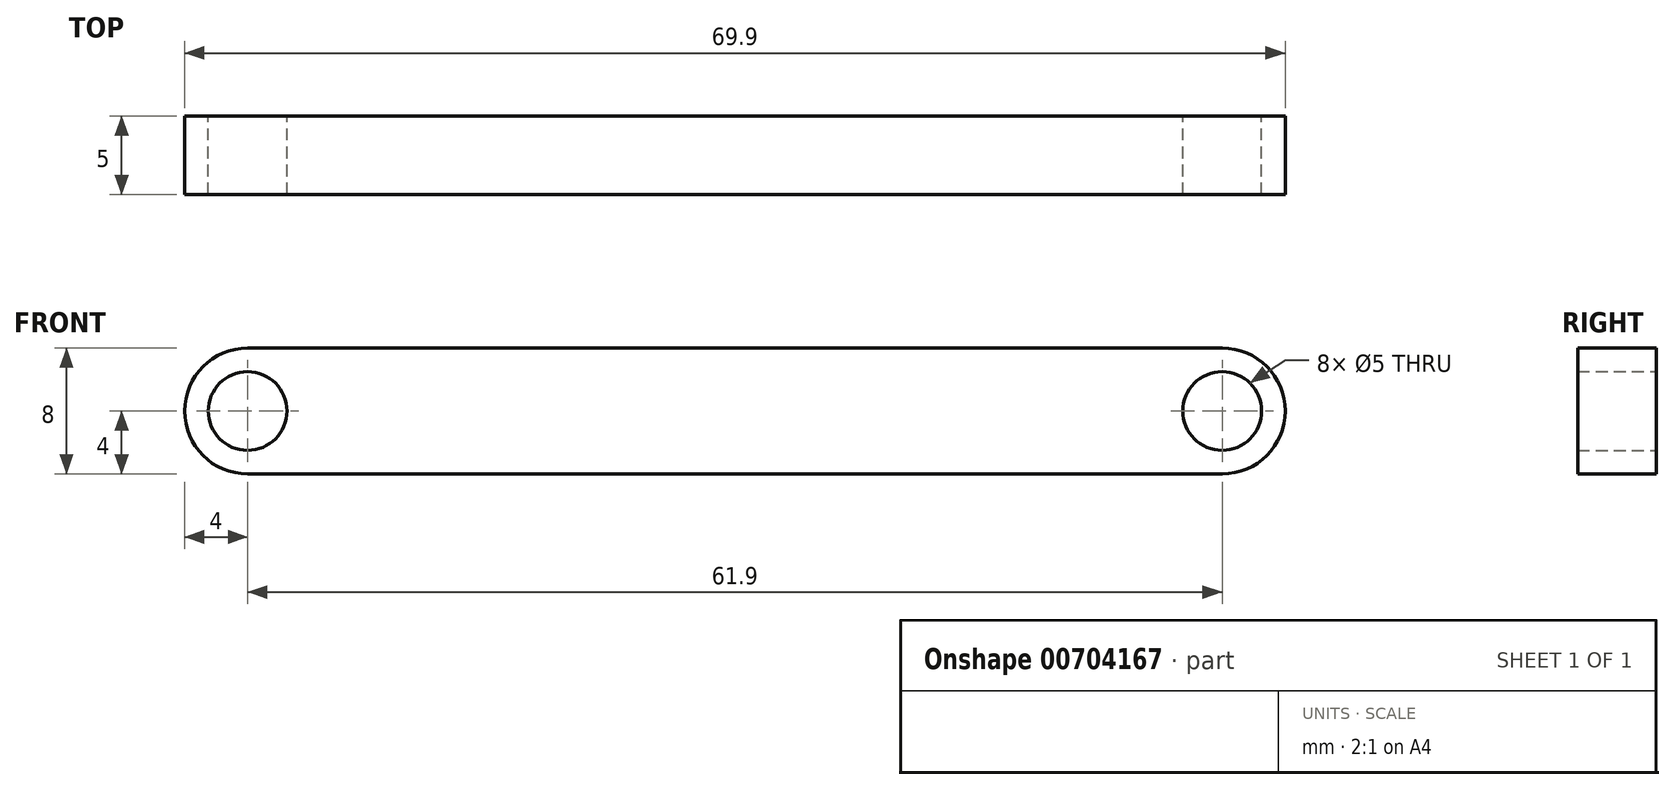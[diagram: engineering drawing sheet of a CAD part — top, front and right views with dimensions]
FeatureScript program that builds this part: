
annotation { "Feature Type Name" : "Feature", "Feature Type Description" : "" }
export const myFeature = defineFeature(function(context is Context, id is Id, definition is map)
    precondition{}
    {
        {
            var Q0;
            Q0=qCreatedBy(makeId("Front.planeOp"),FACE);
            var sketch = newSketch(context, id + "F0", { "sketchPlane" : qUnion([Q0])});
            skLineSegment(sketch, "E0.bottom", {"start": v(-30.95, 4) * mm, "end": v(0, 4) * mm});
            skLineSegment(sketch, "E0.top", {"start": v(-30.95, -4) * mm, "end": v(0, -4) * mm});
            skLineSegment(sketch, "E0.left", {"start": v(-30.95, 4) * mm, "end": v(-30.95, -4) * mm, "construction": true});
            skLineSegment(sketch, "E0.right", {"start": v(0, 4) * mm, "end": v(0, -4) * mm});
            skArc(sketch, "E1", {"start": v(-30.95, -4) * mm, "mid": v(-34.95, 0) * mm, "end": v(-30.95, 4) * mm});
            skCircle(sketch, "E2", {"center": v(-30.95, 0) * mm, "radius": 2.5 * mm});
            skLineSegment(sketch, "E3.MirrorCS", {"start": v(30.95, -4) * mm, "end": v(0, -4) * mm});
            skArc(sketch, "E4.MirrorCS", {"start": v(30.95, -4) * mm, "mid": v(34.95, 0) * mm, "end": v(30.95, 4) * mm});
            skCircle(sketch, "E5.MirrorC", {"center": v(30.95, 0) * mm, "radius": 2.5 * mm});
            skLineSegment(sketch, "E6.MirrorCS", {"start": v(30.95, 4) * mm, "end": v(0, 4) * mm});
            skSolve(sketch);
        }
        {
            var Q0;
            Q0=makeQuery(id+"F0.imprint","IMPRINT",FACE,{"disambiguationData":[TD([[makeQuery(id+"F0.imprint","IMPRINT",EDGE,{"derivedFrom":sQuery(id+"F0.wireOp",EDGE,"E0.bottom")}),-1.0]])]});
            var Q1;
            Q1=makeQuery(id+"F0.imprint","IMPRINT",FACE,{"disambiguationData":[TD([[makeQuery(id+"F0.imprint","IMPRINT",EDGE,{"derivedFrom":sQuery(id+"F0.wireOp",EDGE,"E0.right")}),1.0]])]});
            extrude(context, id + "F1", {"entities" : qUnion([Q0, Q1]), "depth" : 5 * mm, "offsetDistance" : 25 * mm});
        }
    });
